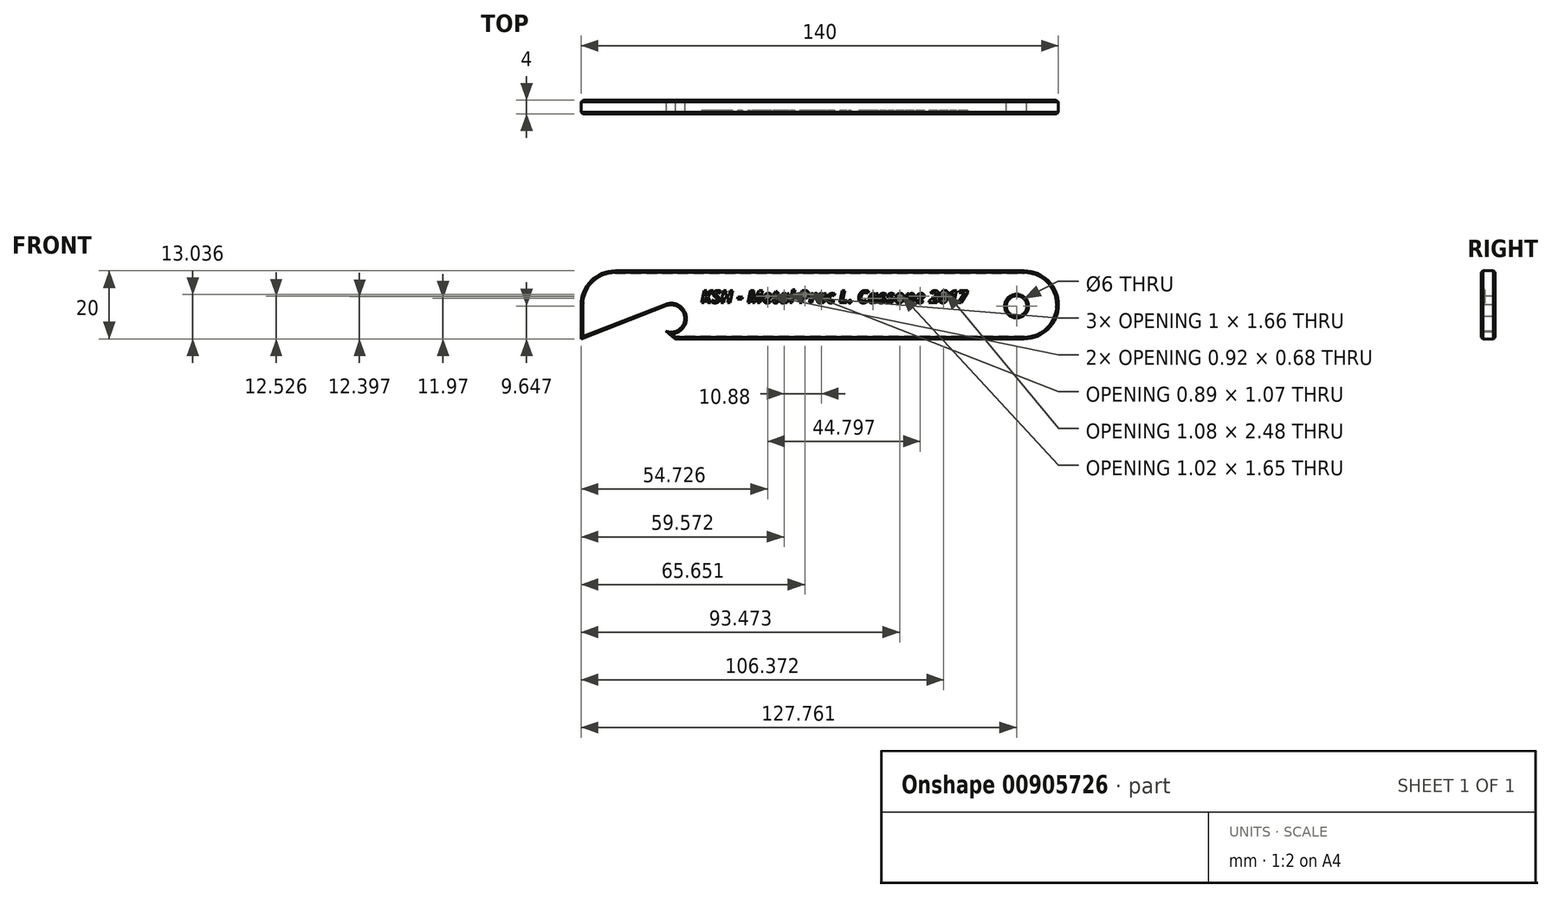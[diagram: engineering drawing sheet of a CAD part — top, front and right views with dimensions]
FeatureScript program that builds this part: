
annotation { "Feature Type Name" : "Feature", "Feature Type Description" : "" }
export const myFeature = defineFeature(function(context is Context, id is Id, definition is map)
    precondition{}
    {
        {
            var Q0;
            Q0=qCreatedBy(makeId("Front.planeOp"),FACE);
            var sketch = newSketch(context, id + "F0", { "sketchPlane" : qUnion([Q0])});
            skLineSegment(sketch, "E0.bottom", {"start": v(-44.29, -22.06) * mm, "end": v(95.71, -22.06) * mm});
            skLineSegment(sketch, "E0.top", {"start": v(-44.29, -2.06) * mm, "end": v(95.71, -2.06) * mm});
            skLineSegment(sketch, "E0.left", {"start": v(-44.29, -22.06) * mm, "end": v(-44.29, -2.06) * mm});
            skLineSegment(sketch, "E0.right", {"start": v(95.71, -22.06) * mm, "end": v(95.71, -2.06) * mm});
            skCircle(sketch, "E1", {"center": v(83.47, -12.41) * mm, "radius": 3 * mm});
            skSolve(sketch);
        }
        {
            var Q0;
            Q0=makeQuery(id+"F0.imprint","IMPRINT",FACE,{"disambiguationData":[TD([[makeQuery(id+"F0.imprint","IMPRINT",EDGE,{"derivedFrom":sQuery(id+"F0.wireOp",EDGE,"E0.bottom")}),1.0]])]});
            extrude(context, id + "F1", {"entities" : qUnion([Q0]), "depth" : 4 * mm, "offsetDistance" : 25 * mm});
        }
        {
            var Q0;
            Q0=makeQuery(id+"F1.opExtrude","CAP_FACE",FACE,{"disambiguationData":[OSD([sQuery(id+"F0.wireOp",EDGE,"E0.bottom"),sQuery(id+"F0.wireOp",EDGE,"E0.top"),sQuery(id+"F0.wireOp",EDGE,"E0.left"),sQuery(id+"F0.wireOp",EDGE,"E0.right")])],"isStart":false});
            var sketch = newSketch(context, id + "F2", { "sketchPlane" : qUnion([Q0])});
            skArc(sketch, "E2", {"start": v(85.71, -22.06) * mm, "mid": v(95.71, -12.06) * mm, "end": v(85.71, -2.06) * mm});
            skPoint(sketch, "E3", {"position": v(-44.29, -12.06) * mm});
            skPoint(sketch, "E4", {"position": v(-34.29, -2.06) * mm});
            skPoint(sketch, "E5", {"position": v(-34.29, -12.06) * mm});
            skArc(sketch, "E6", {"start": v(-34.29, -2.06) * mm, "mid": v(-41.36, -4.99) * mm, "end": v(-44.29, -12.06) * mm});
            skCircle(sketch, "E7", {"center": v(-17.9, -16.06) * mm, "radius": 4 * mm});
            skLineSegment(sketch, "E8", {"start": v(-44.29, -22.06) * mm, "end": v(-19.35, -12.33) * mm});
            skLineSegment(sketch, "E9", {"start": v(-19.35, -19.78) * mm, "end": v(-16.68, -22.06) * mm});
            skSolve(sketch);
        }
        {
            var Q0;
            {var subQ0=sQuery(id+"F2.wireOp",EDGE,"E2");var subQ1=makeQuery(id+"F1.opExtrude","CAP_EDGE",EDGE,{"disambiguationData":[OSD([sQuery(id+"F0.wireOp",EDGE,"E0.bottom")])],"isStart":false});var subQ2=makeQuery(id+"F2.imprint","INTERSECT",VERTEX,{"derivedFrom":[subQ1,subQ0]});Q0=makeQuery(id+"F2.imprint","IMPRINT",FACE,{"disambiguationData":[TD([[makeQuery(id+"F2.imprint","IMPRINT",EDGE,{"disambiguationData":[TD([[subQ2,-1.0]])],"derivedFrom":subQ0}),-1.0]])]});}
            var Q1;
            {var subQ0=sQuery(id+"F2.wireOp",EDGE,"E2");var subQ1=makeQuery(id+"F1.opExtrude","CAP_EDGE",EDGE,{"disambiguationData":[OSD([sQuery(id+"F0.wireOp",EDGE,"E0.top")])],"isStart":false});var subQ2=makeQuery(id+"F2.imprint","INTERSECT",VERTEX,{"derivedFrom":[subQ1,subQ0]});Q1=makeQuery(id+"F2.imprint","IMPRINT",FACE,{"disambiguationData":[TD([[makeQuery(id+"F2.imprint","IMPRINT",EDGE,{"disambiguationData":[TD([[subQ2,1.0]])],"derivedFrom":subQ0}),-1.0]])]});}
            var Q2;
            {var subQ0=sQuery(id+"F2.wireOp",EDGE,"E6");Q2=makeQuery(id+"F2.imprint","IMPRINT",FACE,{"disambiguationData":[TD([[makeQuery(id+"F2.imprint","IMPRINT",EDGE,{"derivedFrom":subQ0}),-1.0]])]});}
            extrude(context, id + "F3", {"entities" : qUnion([Q0, Q1, Q2]), "operationType" : NewBodyOperationType.REMOVE, "endBound" : BoundingType.THROUGH_ALL, "oppositeDirection" : true, "depth" : 25 * mm, "offsetDistance" : 25 * mm});
        }
        {
            var Q0;
            {var subQ0=sQuery(id+"F2.wireOp",EDGE,"E8");Q0=makeQuery(id+"F2.imprint","IMPRINT",FACE,{"disambiguationData":[TD([[makeQuery(id+"F2.imprint","IMPRINT",EDGE,{"derivedFrom":subQ0}),-1.0]])]});}
            extrude(context, id + "F4", {"entities" : qUnion([Q0]), "operationType" : NewBodyOperationType.REMOVE, "oppositeDirection" : true, "depth" : 25 * mm, "offsetDistance" : 25 * mm});
        }
        {
            var Q0;
            {var subQ0=sQuery(id+"F2.wireOp",EDGE,"E7");var subQ1=makeQuery(id+"F2.imprint","INTERSECT",VERTEX,{"derivedFrom":[subQ0,sQuery(id+"F2.wireOp",EDGE,"E8")]});Q0=makeQuery(id+"F2.imprint","IMPRINT",FACE,{"disambiguationData":[TD([[makeQuery(id+"F2.imprint","IMPRINT",EDGE,{"disambiguationData":[TD([[subQ1,-1.0]])],"derivedFrom":subQ0}),1.0]])]});}
            extrude(context, id + "F5", {"entities" : qUnion([Q0]), "operationType" : NewBodyOperationType.REMOVE, "endBound" : BoundingType.THROUGH_ALL, "oppositeDirection" : true, "depth" : 25 * mm, "offsetDistance" : 25 * mm});
        }
        {
            var Q0;
            Q0=makeQuery(id+"F1.opExtrude","CAP_FACE",FACE,{"disambiguationData":[OSD([sQuery(id+"F0.wireOp",EDGE,"E0.bottom"),sQuery(id+"F0.wireOp",EDGE,"E0.top"),sQuery(id+"F0.wireOp",EDGE,"E0.left"),sQuery(id+"F0.wireOp",EDGE,"E0.right"),sQuery(id+"F0.wireOp",EDGE,"E1")])],"isStart":false});
            var Q1;
            {var subQ0=sQuery(id+"F2.wireOp",EDGE,"E2");var subQ1=sQuery(id+"F0.wireOp",EDGE,"E0.top");var subQ2=sQuery(id+"F0.wireOp",EDGE,"E0.right");var subQ4=sQuery(id+"F0.wireOp",EDGE,"E0.bottom");Q1=makeQuery(id+"F3.boolean.opBoolean","INTERSECT",EDGE,{"derivedFrom":[makeQuery(id+"F1.opExtrude","CAP_FACE",FACE,{"disambiguationData":[OSD([subQ4,subQ1,sQuery(id+"F0.wireOp",EDGE,"E0.left"),subQ2,sQuery(id+"F0.wireOp",EDGE,"E1")])],"isStart":true}),makeQuery(id+"F3.opExtrude","SWEPT_FACE",FACE,{"disambiguationData":[OSD([subQ0]),TDD([makeQuery(id+"F2.imprint","IMPRINT",EDGE,{"disambiguationData":[TD([[makeQuery(id+"F2.imprint","INTERSECT",VERTEX,{"derivedFrom":[makeQuery(id+"F1.opExtrude","CAP_EDGE",EDGE,{"disambiguationData":[OSD([subQ4])],"isStart":false}),subQ0]}),-1.0]])],"derivedFrom":subQ0})])]}),makeQuery(id+"F3.opExtrude","SWEPT_FACE",FACE,{"disambiguationData":[OSD([subQ0]),TDD([makeQuery(id+"F2.imprint","IMPRINT",EDGE,{"disambiguationData":[TD([[makeQuery(id+"F2.imprint","INTERSECT",VERTEX,{"derivedFrom":[makeQuery(id+"F1.opExtrude","CAP_EDGE",EDGE,{"disambiguationData":[OSD([subQ1])],"isStart":false}),subQ0]}),1.0]])],"derivedFrom":subQ0})])]})]});}
            var Q2;
            {var subQ0=sQuery(id+"F2.wireOp",EDGE,"E2");Q2=makeQuery(id+"F3.boolean.opBoolean","MERGE",EDGE,{"derivedFrom":[],"fromTools":[makeQuery(id+"F3.opExtrude","CAP_EDGE",EDGE,{"disambiguationData":[OSD([subQ0]),TDD([makeQuery(id+"F2.imprint","IMPRINT",EDGE,{"disambiguationData":[TD([[makeQuery(id+"F2.imprint","INTERSECT",VERTEX,{"derivedFrom":[makeQuery(id+"F1.opExtrude","CAP_EDGE",EDGE,{"disambiguationData":[OSD([sQuery(id+"F0.wireOp",EDGE,"E0.bottom")])],"isStart":false}),subQ0]}),-1.0]])],"derivedFrom":subQ0})])],"isStart":true}),makeQuery(id+"F3.opExtrude","CAP_EDGE",EDGE,{"disambiguationData":[OSD([subQ0]),TDD([makeQuery(id+"F2.imprint","IMPRINT",EDGE,{"disambiguationData":[TD([[makeQuery(id+"F2.imprint","INTERSECT",VERTEX,{"derivedFrom":[makeQuery(id+"F1.opExtrude","CAP_EDGE",EDGE,{"disambiguationData":[OSD([sQuery(id+"F0.wireOp",EDGE,"E0.top")])],"isStart":false}),subQ0]}),1.0]])],"derivedFrom":subQ0})])],"isStart":true})]});}
            chamfer(context, id + "F6", {"entities" : qUnion([Q0, Q1, Q2]), "width" : 0.5 * mm, "tangentPropagation" : true});
        }
        {
            var Q0;
            Q0=makeQuery(id+"F1.opExtrude","CAP_FACE",FACE,{"disambiguationData":[OSD([sQuery(id+"F0.wireOp",EDGE,"E0.bottom"),sQuery(id+"F0.wireOp",EDGE,"E0.top"),sQuery(id+"F0.wireOp",EDGE,"E0.left"),sQuery(id+"F0.wireOp",EDGE,"E0.right"),sQuery(id+"F0.wireOp",EDGE,"E1")])],"isStart":true});
            chamfer(context, id + "F7", {"entities" : qUnion([Q0]), "width" : 0.5 * mm, "tangentPropagation" : true});
        }
        {
            var Q0;
            Q0=makeQuery(id+"F1.opExtrude","CAP_FACE",FACE,{"disambiguationData":[OSD([sQuery(id+"F0.wireOp",EDGE,"E0.bottom"),sQuery(id+"F0.wireOp",EDGE,"E0.top"),sQuery(id+"F0.wireOp",EDGE,"E0.left"),sQuery(id+"F0.wireOp",EDGE,"E0.right"),sQuery(id+"F0.wireOp",EDGE,"E1")])],"isStart":false});
            var sketch = newSketch(context, id + "F8", { "sketchPlane" : qUnion([Q0])});
            skText(sketch, "E10", { "text": "KSH - Metal Prac L. Cassone 2017", "fontName": "OpenSans-BoldItalic.ttf"});
            const initialGuessF8  = {"E10": [-0.0091, -0.01147, 1, 0, 0.00364]};
            skSetInitialGuess(sketch, initialGuessF8);
            skSolve(sketch);
        }
        {
            var Q0;
            Q0 = qSketchRegion(id + "F8", true);
            extrude(context, id + "F9", {"entities" : qUnion([Q0]), "oppositeDirection" : true, "depth" : 1 * mm, "offsetDistance" : 25 * mm});
        }
    });
